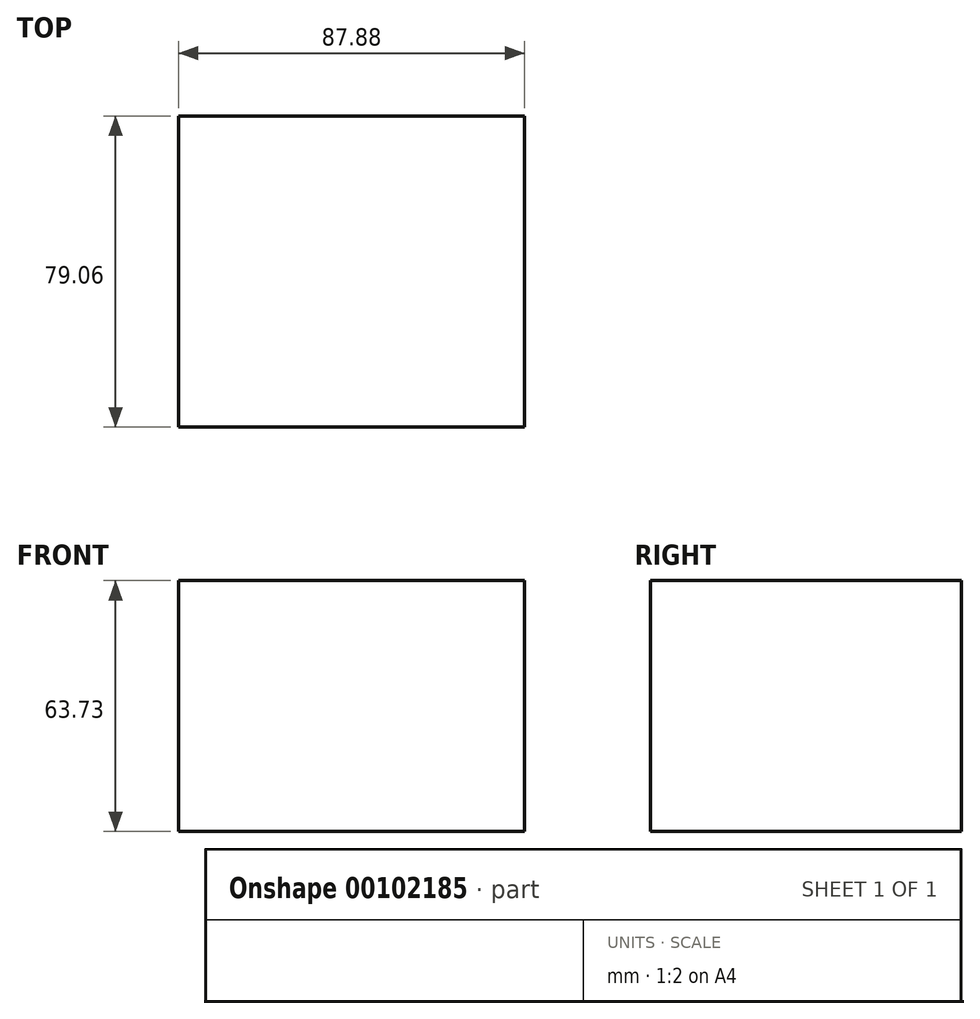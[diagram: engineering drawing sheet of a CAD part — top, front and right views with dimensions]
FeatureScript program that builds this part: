
annotation { "Feature Type Name" : "Feature", "Feature Type Description" : "" }
export const myFeature = defineFeature(function(context is Context, id is Id, definition is map)
    precondition{}
    {
        {
            var Q0;
            Q0=qCreatedBy(makeId("Front.planeOp"),FACE);
            var sketch = newSketch(context, id + "F0", { "sketchPlane" : qUnion([Q0])});
            skLineSegment(sketch, "E0.bottom", {"start": v(-45.43, 29.3) * mm, "end": v(42.45, 29.3) * mm});
            skLineSegment(sketch, "E0.top", {"start": v(-45.43, -34.44) * mm, "end": v(42.45, -34.44) * mm});
            skLineSegment(sketch, "E0.left", {"start": v(-45.43, 29.3) * mm, "end": v(-45.43, -34.44) * mm});
            skLineSegment(sketch, "E0.right", {"start": v(42.45, 29.3) * mm, "end": v(42.45, -34.44) * mm});
            skSolve(sketch);
        }
        {
            var Q0;
            Q0=makeQuery(id+"F0.imprint","IMPRINT",FACE,{"disambiguationData":[TD([[makeQuery(id+"F0.imprint","IMPRINT",EDGE,{"derivedFrom":sQuery(id+"F0.wireOp",EDGE,"E0.bottom")}),-1.0]])]});
            extrude(context, id + "F1", {"entities" : qUnion([Q0]), "depth" : 79.06 * mm});
        }
    });
